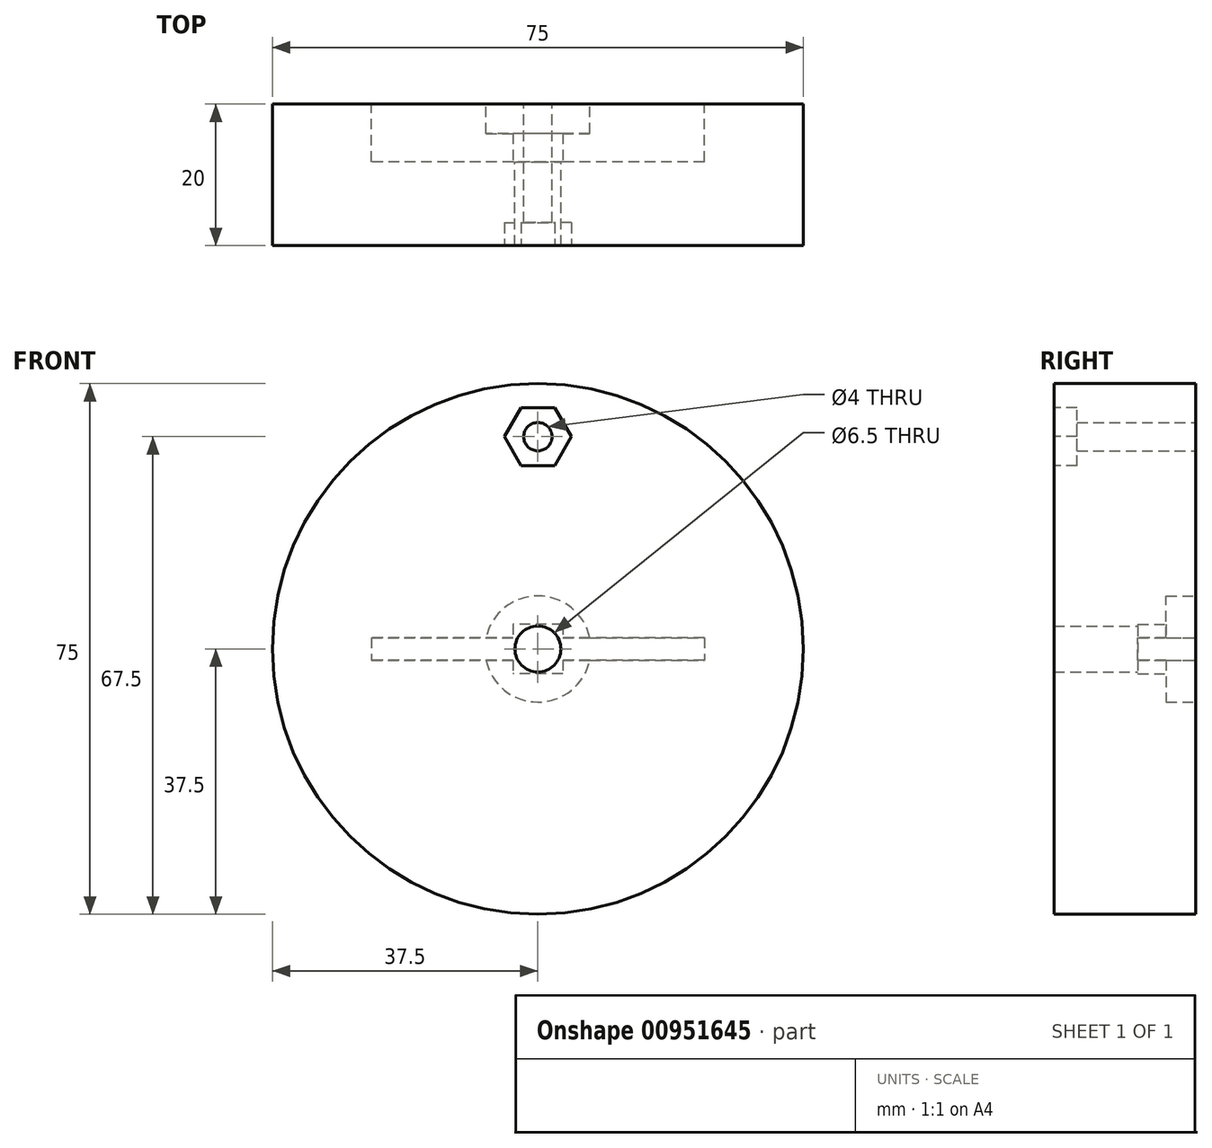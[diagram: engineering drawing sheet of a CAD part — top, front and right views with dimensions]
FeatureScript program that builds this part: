
annotation { "Feature Type Name" : "Feature", "Feature Type Description" : "" }
export const myFeature = defineFeature(function(context is Context, id is Id, definition is map)
    precondition{}
    {
        {
            var Q0;
            Q0=qCreatedBy(makeId("Front.planeOp"),FACE);
            var sketch = newSketch(context, id + "F0", { "sketchPlane" : qUnion([Q0])});
            skCircle(sketch, "E0", {"center": v(0, 0) * mm, "radius": 37.5 * mm});
            skSolve(sketch);
        }
        {
            var Q0;
            Q0 = qSketchRegion(id + "F0", true);
            extrude(context, id + "F1", {"entities" : qUnion([Q0]), "depth" : 20 * mm, "offsetDistance" : 25 * mm});
        }
        {
            var Q0;
            Q0=qCreatedBy(makeId("Front.planeOp"),FACE);
            var sketch = newSketch(context, id + "F2", { "sketchPlane" : qUnion([Q0])});
            skCircle(sketch, "E1", {"center": v(0, 30) * mm, "radius": 2 * mm});
            skSolve(sketch);
        }
        {
            var Q0;
            Q0 = qSketchRegion(id + "F2", true);
            extrude(context, id + "F3", {"entities" : qUnion([Q0]), "operationType" : NewBodyOperationType.REMOVE, "endBound" : BoundingType.THROUGH_ALL, "depth" : 25 * mm, "offsetDistance" : 25 * mm});
        }
        {
            var Q0;
            Q0=makeQuery(id+"F1.opExtrude","CAP_FACE",FACE,{"disambiguationData":[OSD([sQuery(id+"F0.wireOp",EDGE,"E0")])],"isStart":false});
            var sketch = newSketch(context, id + "F4", { "sketchPlane" : qUnion([Q0])});
            skCircle(sketch, "E2.cCircle", {"center": v(0, 30) * mm, "radius": 4.11 * mm, "construction": true});
            skLineSegment(sketch, "E2.0", {"start": v(-2.37, 34.11) * mm, "end": v(2.37, 34.11) * mm});
            skLineSegment(sketch, "E2.1", {"start": v(2.37, 34.11) * mm, "end": v(4.75, 30) * mm});
            skLineSegment(sketch, "E2.2", {"start": v(4.75, 30) * mm, "end": v(2.37, 25.89) * mm});
            skLineSegment(sketch, "E2.3", {"start": v(2.37, 25.89) * mm, "end": v(-2.37, 25.89) * mm});
            skLineSegment(sketch, "E2.4", {"start": v(-2.37, 25.89) * mm, "end": v(-4.75, 30) * mm});
            skLineSegment(sketch, "E2.5", {"start": v(-4.75, 30) * mm, "end": v(-2.37, 34.11) * mm});
            skPoint(sketch, "E2.0.midPoint", {"position": v(0, 34.11) * mm});
            skSolve(sketch);
        }
        {
            var Q0;
            Q0 = qSketchRegion(id + "F4", true);
            extrude(context, id + "F5", {"entities" : qUnion([Q0]), "operationType" : NewBodyOperationType.REMOVE, "oppositeDirection" : true, "depth" : 3.25 * mm, "offsetDistance" : 25 * mm});
        }
        {
            var Q0;
            Q0=makeQuery(id+"F1.opExtrude","CAP_FACE",FACE,{"disambiguationData":[OSD([sQuery(id+"F0.wireOp",EDGE,"E0")])],"isStart":true});
            var sketch = newSketch(context, id + "F6", { "sketchPlane" : qUnion([Q0])});
            skCircle(sketch, "E3", {"center": v(0, 0) * mm, "radius": 7.5 * mm});
            skSolve(sketch);
        }
        {
            var Q0;
            Q0 = qSketchRegion(id + "F6", true);
            extrude(context, id + "F7", {"entities" : qUnion([Q0]), "operationType" : NewBodyOperationType.REMOVE, "oppositeDirection" : true, "depth" : 4.15 * mm, "offsetDistance" : 25 * mm});
        }
        {
            var Q0;
            Q0=makeQuery(id+"F7.boolean.opBoolean","COPY",FACE,{"derivedFrom":makeQuery(id+"F7.opExtrude","CAP_FACE",FACE,{"disambiguationData":[OSD([sQuery(id+"F6.wireOp",EDGE,"E3")])],"isStart":false})});
            var sketch = newSketch(context, id + "F8", { "sketchPlane" : qUnion([Q0])});
            skLineSegment(sketch, "E4.bottom", {"start": v(-3.5, 3.5) * mm, "end": v(3.5, 3.5) * mm});
            skLineSegment(sketch, "E4.top", {"start": v(-3.5, -3.5) * mm, "end": v(3.5, -3.5) * mm});
            skLineSegment(sketch, "E4.left", {"start": v(-3.5, 3.5) * mm, "end": v(-3.5, -3.5) * mm});
            skLineSegment(sketch, "E4.right", {"start": v(3.5, 3.5) * mm, "end": v(3.5, -3.5) * mm});
            skPoint(sketch, "E4.middle", {"position": v(0, 0) * mm});
            skSolve(sketch);
        }
        {
            var Q0;
            Q0 = qSketchRegion(id + "F8", true);
            extrude(context, id + "F9", {"entities" : qUnion([Q0]), "operationType" : NewBodyOperationType.REMOVE, "oppositeDirection" : true, "depth" : 4 * mm, "offsetDistance" : 25 * mm});
        }
        {
            var Q0;
            Q0=makeQuery(id+"F1.opExtrude","CAP_FACE",FACE,{"disambiguationData":[OSD([sQuery(id+"F0.wireOp",EDGE,"E0")])],"isStart":true});
            var sketch = newSketch(context, id + "F10", { "sketchPlane" : qUnion([Q0])});
            skLineSegment(sketch, "E5.bottom", {"start": v(23.5, 1.59) * mm, "end": v(-23.5, 1.59) * mm});
            skLineSegment(sketch, "E5.top", {"start": v(23.5, -1.59) * mm, "end": v(-23.5, -1.59) * mm});
            skLineSegment(sketch, "E5.left", {"start": v(23.5, 1.59) * mm, "end": v(23.5, -1.6) * mm});
            skLineSegment(sketch, "E5.right", {"start": v(-23.5, 1.59) * mm, "end": v(-23.5, -1.6) * mm});
            skPoint(sketch, "E5.middle", {"position": v(0, 0) * mm});
            skSolve(sketch);
        }
        {
            var Q0;
            Q0 = qSketchRegion(id + "F10", true);
            var Q1;
            Q1=makeQuery(id+"F9.boolean.opBoolean","COPY",FACE,{"derivedFrom":makeQuery(id+"F9.opExtrude","CAP_FACE",FACE,{"disambiguationData":[OSD([sQuery(id+"F8.wireOp",EDGE,"E4.bottom"),sQuery(id+"F8.wireOp",EDGE,"E4.top"),sQuery(id+"F8.wireOp",EDGE,"E4.left"),sQuery(id+"F8.wireOp",EDGE,"E4.right")])],"isStart":false})});
            extrude(context, id + "F11", {"entities" : qUnion([Q0]), "operationType" : NewBodyOperationType.REMOVE, "endBound" : BoundingType.UP_TO_SURFACE, "oppositeDirection" : true, "depth" : 25 * mm, "endBoundEntityFace" : qUnion([Q1]), "offsetDistance" : 25 * mm});
        }
        {
            var Q0;
            Q0=makeQuery(id+"F11.boolean.opBoolean","MERGE",FACE,{"derivedFrom":[makeQuery(id+"F9.boolean.opBoolean","COPY",FACE,{"derivedFrom":makeQuery(id+"F9.opExtrude","CAP_FACE",FACE,{"disambiguationData":[OSD([sQuery(id+"F8.wireOp",EDGE,"E4.bottom"),sQuery(id+"F8.wireOp",EDGE,"E4.top"),sQuery(id+"F8.wireOp",EDGE,"E4.left"),sQuery(id+"F8.wireOp",EDGE,"E4.right")])],"isStart":false})})],"fromTools":[makeQuery(id+"F11.opExtrude","CAP_FACE",FACE,{"disambiguationData":[OSD([sQuery(id+"F10.wireOp",EDGE,"E5.bottom"),sQuery(id+"F10.wireOp",EDGE,"E5.top"),sQuery(id+"F10.wireOp",EDGE,"E5.left"),sQuery(id+"F10.wireOp",EDGE,"E5.right")])],"isStart":false})]});
            var sketch = newSketch(context, id + "F12", { "sketchPlane" : qUnion([Q0])});
            skCircle(sketch, "E6", {"center": v(0, 0) * mm, "radius": 3.25 * mm});
            skSolve(sketch);
        }
        {
            var Q0;
            Q0 = qSketchRegion(id + "F12", true);
            extrude(context, id + "F13", {"entities" : qUnion([Q0]), "operationType" : NewBodyOperationType.REMOVE, "endBound" : BoundingType.THROUGH_ALL, "oppositeDirection" : true, "depth" : 25 * mm, "offsetDistance" : 25 * mm});
        }
    });
